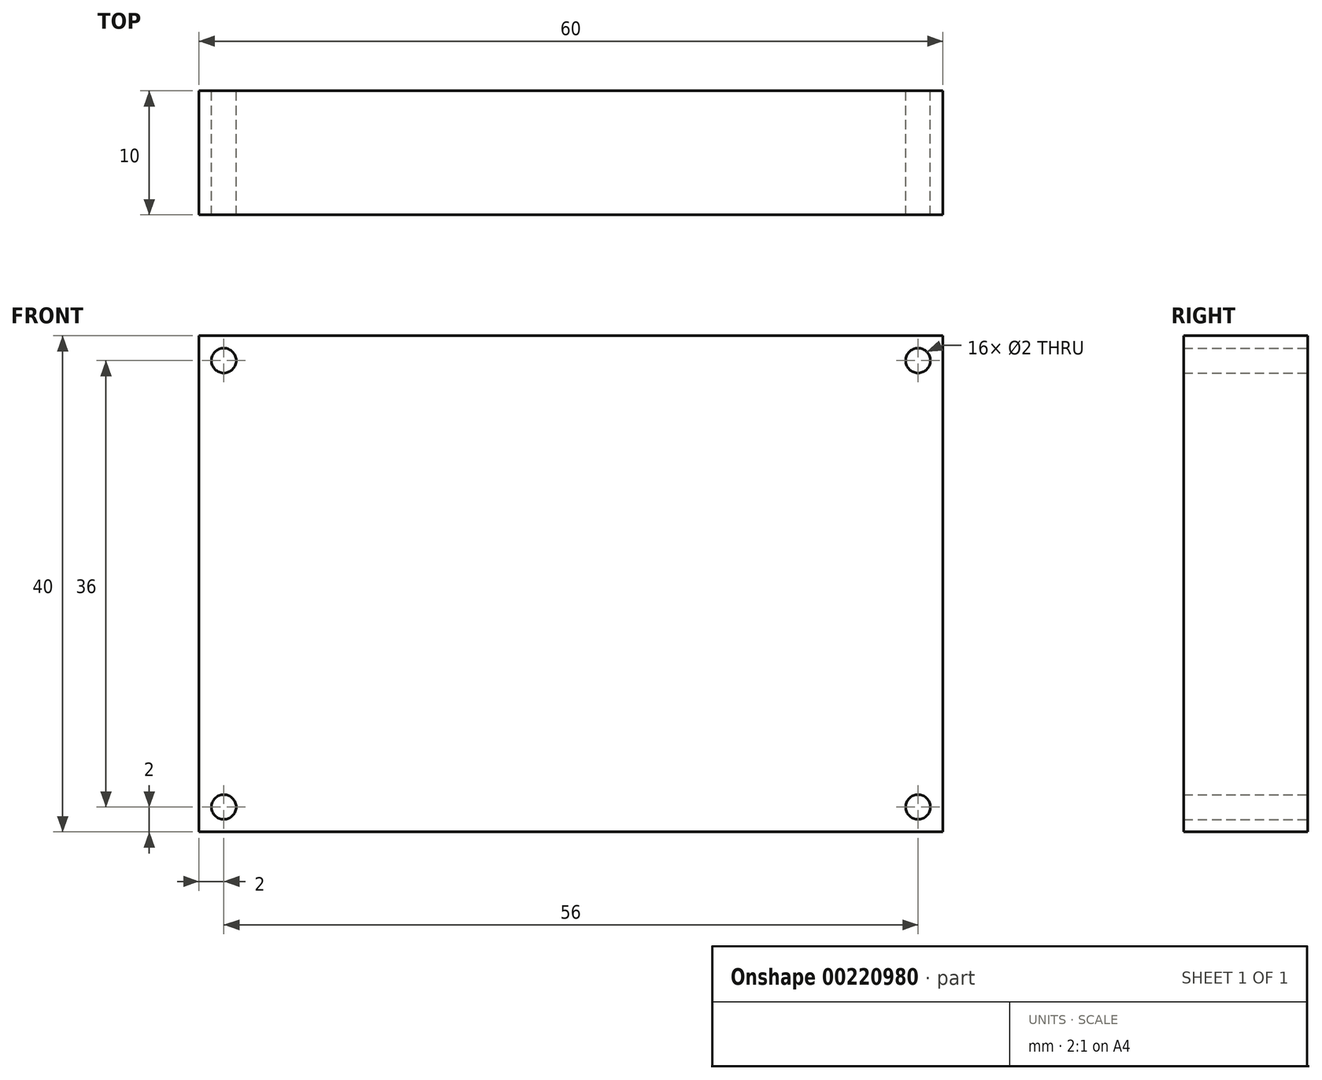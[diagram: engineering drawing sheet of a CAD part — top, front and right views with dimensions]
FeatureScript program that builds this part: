
annotation { "Feature Type Name" : "Feature", "Feature Type Description" : "" }
export const myFeature = defineFeature(function(context is Context, id is Id, definition is map)
    precondition{}
    {
        {
            var Q0;
            Q0=qCreatedBy(makeId("Front.planeOp"),FACE);
            var sketch = newSketch(context, id + "F0", { "sketchPlane" : qUnion([Q0])});
            skLineSegment(sketch, "E0.bottom", {"start": v(30, 20) * mm, "end": v(-30, 20) * mm});
            skLineSegment(sketch, "E0.top", {"start": v(30, -20) * mm, "end": v(-30, -20) * mm});
            skLineSegment(sketch, "E0.left", {"start": v(30, 20) * mm, "end": v(30, -20) * mm});
            skLineSegment(sketch, "E0.right", {"start": v(-30, 20) * mm, "end": v(-30, -20) * mm});
            skPoint(sketch, "E0.middle", {"position": v(0, 0) * mm});
            skLineSegment(sketch, "E1", {"start": v(-30, -20) * mm, "end": v(-28, -20) * mm});
            skLineSegment(sketch, "E2", {"start": v(-28, -20) * mm, "end": v(-28, -18) * mm});
            skCircle(sketch, "E3", {"center": v(-28, -18) * mm, "radius": 1 * mm});
            skLineSegment(sketch, "E4", {"start": v(-28, -18) * mm, "end": v(-28, 18) * mm});
            skLineSegment(sketch, "E5", {"start": v(-28, 18) * mm, "end": v(28, 18) * mm});
            skLineSegment(sketch, "E6", {"start": v(-28, -18) * mm, "end": v(28, -18) * mm});
            skCircle(sketch, "E7", {"center": v(-28, 18) * mm, "radius": 1 * mm});
            skCircle(sketch, "E8", {"center": v(28, 18) * mm, "radius": 1 * mm});
            skCircle(sketch, "E9", {"center": v(28, -18) * mm, "radius": 1 * mm});
            skSolve(sketch);
        }
        {
            var Q0;
            Q0 = qSketchRegion(id + "F0", true);
            extrude(context, id + "F1", {"entities" : qUnion([Q0]), "depth" : 10 * mm});
        }
    });
